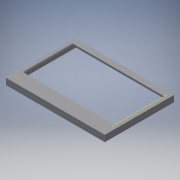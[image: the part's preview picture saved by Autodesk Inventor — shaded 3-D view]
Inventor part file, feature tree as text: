
AUTODESK INVENTOR PART (.ipt)
format: ipt  version: 2017 SP1 (Build 210196100, 196)  size: 203,264 bytes
history: native  units: mm
features: sketch x5, extrude x5, reference x5, projected_geometry x5, plane x3, other x3
ambient origin geometry x8: Origin, YZ Plane, XZ Plane, XY Plane, X Axis, Y Axis, Z Axis, Center Point
bodies: Volumenkörper1 (feature_tree)
feature tree (26):
  plane  "Arbeitsebene1"
  sketch  "Skizze1"  dims[d0=0.15mm d1=0.15mm]
  plane  "Arbeitsebene2"
  extrude  "Extrusion1"  Depth=0.15mm
  extrude  "Extrusion2"  Depth=0.3mm
  extrude  "Extrusion3"  Depth=0.3mm
  extrude  "Extrusion4"  Depth=1.5mm
  sketch  "Skizze5"  dims[d11=2.5mm d12=10.0mm d13=0.0mm d14=0.2mm d15=1.0mm d16=1.2mm d17=2.5mm d18=0.2mm d19=1.2mm d20=2.5mm d21=10.0mm d22=0.0mm d23=10.0mm d24=0.0mm d25=10.0mm d26=0.0mm d27=0.3mm d28=0.3mm d29=10.0mm d30=0.0mm]
  plane  "Arbeitsebene3"
  extrude  "Extrusion5"  Depth=2.5mm TaperAngle=0.0deg
  reference  "Referenz1"
  reference  "Referenz2"
  sketch  "Skizze2"  dims[d2=0.2mm d3=0.3mm]
  reference  "Referenz3"
  reference  "Referenz4"
  sketch  "Skizze3"  dims[d5=0.2mm d6=0.3mm]
  projected_geometry  "Projizierte Kontur1"
  projected_geometry  "Projizierte Kontur2"
  sketch  "Skizze4"  dims[d9=1.0mm d10=1.5mm]
  projected_geometry  "Projizierte Kontur3"
  projected_geometry  "Projizierte Kontur4"
  reference  "Referenz5"
  projected_geometry  "Projizierte Kontur5"
  other  "<userpath>\Dropbox\Elektronik\aXe_Dashboard240XL\Gehäuse\DisplayDummyAuschnitt.iam"
  other  "DisplayDummyAuschnitt.iam"
  other  "DisplayDummy:1"
